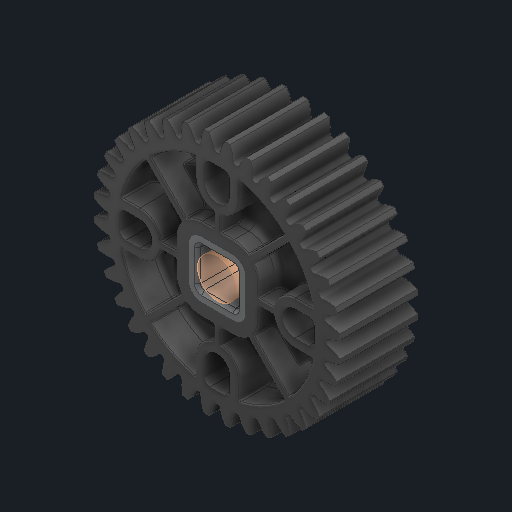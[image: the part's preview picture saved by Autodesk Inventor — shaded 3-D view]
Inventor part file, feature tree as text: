
AUTODESK INVENTOR PART (.ipt)
format: ipt  version: 2025 (Build 290162000, 162)  size: 3,310,592 bytes
history: native  units: in
note: dims shown in document units (in); Inventor stores cm internally (conversion verified against a paired STEP export)
features: other x6, sketch x1
ambient origin geometry x8: Origin, YZ Plane, XZ Plane, XY Plane, X Axis, Y Axis, Z Axis, Center Point
bodies: Solid1 (feature_tree), Solid2 (feature_tree)
feature tree (7):
  other  "HS 36T Gear, No Insert.ipt"
  other  "Solid1::HS 36T Gear, No Insert.ipt"
  other  "Solid2::HS 36T Gear, No Insert.ipt"
  other  "TaggingFeature1"
  sketch  "Sketch1"  dims[d0=0.3937in]
  other  "Srf1"
  other  "Srf1::Derived"
